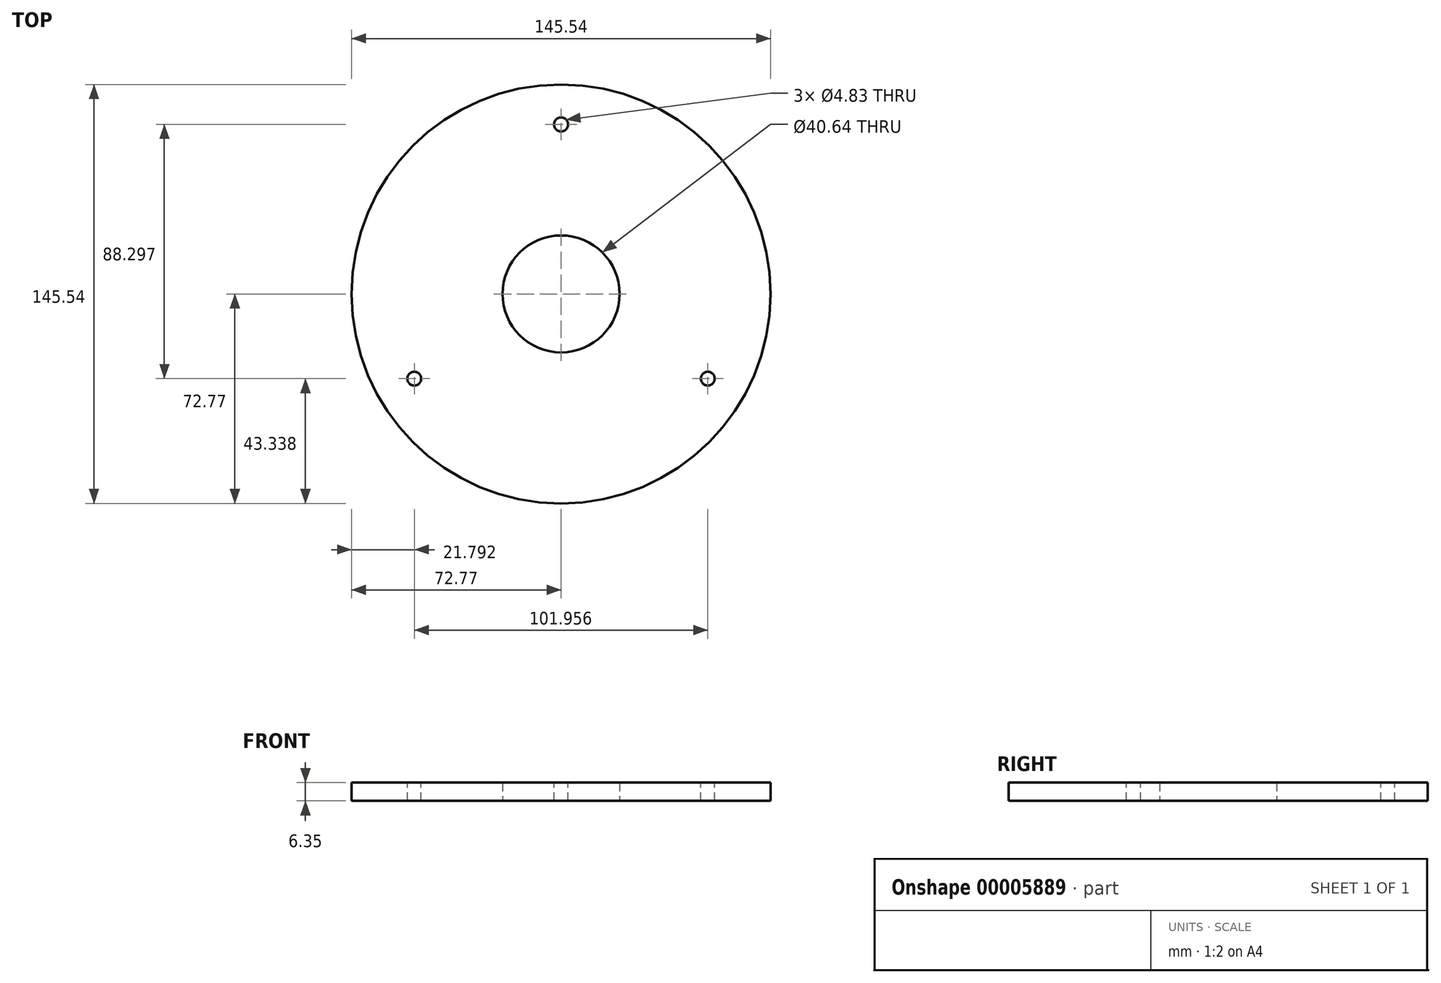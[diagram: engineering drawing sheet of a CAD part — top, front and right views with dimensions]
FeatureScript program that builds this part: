
annotation { "Feature Type Name" : "Feature", "Feature Type Description" : "" }
export const myFeature = defineFeature(function(context is Context, id is Id, definition is map)
    precondition{}
    {
        {
            var Q0;
            Q0=qCreatedBy(makeId("Top.planeOp"),FACE);
            var sketch = newSketch(context, id + "F0", { "sketchPlane" : qUnion([Q0])});
            skCircle(sketch, "E0", {"center": v(0, 0) * mm, "radius": 20.32 * mm});
            skLineSegment(sketch, "E1", {"start": v(0, 0) * mm, "end": v(-72.77, 0) * mm, "construction": true});
            skLineSegment(sketch, "E2", {"start": v(-72.77, 0) * mm, "end": v(-148.97, 0) * mm, "construction": true});
            skArc(sketch, "E3", {"start": v(-157.42, 43.64) * mm, "mid": v(-193.42, 0) * mm, "end": v(-157.42, -43.64) * mm});
            skCircle(sketch, "E4", {"center": v(-148.97, 0) * mm, "radius": 4.76 * mm});
            skCircle(sketch, "E5.converted", {"center": v(0, 0) * mm, "radius": 72.77 * mm});
            skSolve(sketch);
        }
        {
            var Q0;
            Q0=makeQuery(id+"F0.imprint","IMPRINT",FACE,{"disambiguationData":[TD([[makeQuery(id+"F0.imprint","IMPRINT",EDGE,{"derivedFrom":sQuery(id+"F0.wireOp",EDGE,"E0")}),-1.0]])]});
            extrude(context, id + "F1", {"entities" : qUnion([Q0]), "depth" : 6.35 * mm});
        }
        {
            var Q0;
            Q0=makeQuery(id+"F1.opExtrude","CAP_FACE",FACE,{"disambiguationData":[OSD([sQuery(id+"F0.wireOp",EDGE,"e6a074b3-585f-481e-9c95-f9684aebe7da"),sQuery(id+"F0.wireOp",EDGE,"E0"),sQuery(id+"F0.wireOp",EDGE,"7409aa68-249a-4d23-94e3-a1b410b62b42")])],"isStart":false});
            var sketch = newSketch(context, id + "F2", { "sketchPlane" : qUnion([Q0])});
            skLineSegment(sketch, "E6", {"start": v(0, 0) * mm, "end": v(0, 72.77) * mm, "construction": true});
            skCircle(sketch, "E7", {"center": v(0, 58.86) * mm, "radius": 4.76 * mm});
            skCircle(sketch, "E8.1.0", {"center": v(-50.98, -29.43) * mm, "radius": 4.76 * mm});
            skCircle(sketch, "E8.2.0", {"center": v(50.98, -29.43) * mm, "radius": 4.76 * mm});
            skPoint(sketch, "E8.center", {"position": v(0, 0) * mm});
            skCircle(sketch, "E9", {"center": v(0, 58.86) * mm, "radius": 2.41 * mm});
            skCircle(sketch, "E10.1.0", {"center": v(-50.98, -29.43) * mm, "radius": 2.41 * mm});
            skCircle(sketch, "E10.2.0", {"center": v(50.98, -29.43) * mm, "radius": 2.41 * mm});
            skSolve(sketch);
        }
        {
            var Q0;
            Q0=makeQuery(id+"F2.imprint","IMPRINT",FACE,{"disambiguationData":[TD([[makeQuery(id+"F2.imprint","IMPRINT",EDGE,{"derivedFrom":sQuery(id+"F2.wireOp",EDGE,"E10.1.0")}),1.0]])]});
            var Q1;
            Q1=makeQuery(id+"F2.imprint","IMPRINT",FACE,{"disambiguationData":[TD([[makeQuery(id+"F2.imprint","IMPRINT",EDGE,{"derivedFrom":sQuery(id+"F2.wireOp",EDGE,"E10.2.0")}),1.0]])]});
            var Q2;
            Q2=makeQuery(id+"F2.imprint","IMPRINT",FACE,{"disambiguationData":[TD([[makeQuery(id+"F2.imprint","IMPRINT",EDGE,{"derivedFrom":sQuery(id+"F2.wireOp",EDGE,"E9")}),1.0]])]});
            extrude(context, id + "F3", {"entities" : qUnion([Q0, Q1, Q2]), "operationType" : NewBodyOperationType.REMOVE, "endBound" : BoundingType.THROUGH_ALL, "oppositeDirection" : true, "depth" : 25.4 * mm});
        }
        {
            var Q0;
            Q0=makeQuery(id+"F1.opExtrude","CAP_FACE",FACE,{"disambiguationData":[OSD([sQuery(id+"F0.wireOp",EDGE,"e6a074b3-585f-481e-9c95-f9684aebe7da"),sQuery(id+"F0.wireOp",EDGE,"E0"),sQuery(id+"F0.wireOp",EDGE,"7409aa68-249a-4d23-94e3-a1b410b62b42")])],"isStart":false});
            var sketch = newSketch(context, id + "F4", { "sketchPlane" : qUnion([Q0])});
            skCircle(sketch, "E11", {"center": v(0, 0) * mm, "radius": 17.78 * mm});
            skSolve(sketch);
        }
        {
            var Q0;
            Q0=makeQuery(id+"F4.imprint","IMPRINT",FACE,{"disambiguationData":[TD([[makeQuery(id+"F4.imprint","IMPRINT",EDGE,{"derivedFrom":sQuery(id+"F4.wireOp",EDGE,"E11")}),1.0]])]});
            extrude(context, id + "F5", {"entities" : qUnion([Q0]), "operationType" : NewBodyOperationType.REMOVE, "oppositeDirection" : true, "depth" : 2.8 * mm});
        }
        {
            var Q0;
            Q0=makeQuery(id+"F1.opExtrude","CAP_FACE",FACE,{"disambiguationData":[OSD([sQuery(id+"F0.wireOp",EDGE,"e6a074b3-585f-481e-9c95-f9684aebe7da"),sQuery(id+"F0.wireOp",EDGE,"E0"),sQuery(id+"F0.wireOp",EDGE,"7409aa68-249a-4d23-94e3-a1b410b62b42")])],"isStart":true});
            var sketch = newSketch(context, id + "F6", { "sketchPlane" : qUnion([Q0])});
            skCircle(sketch, "E12", {"center": v(0, 0) * mm, "radius": 18.41 * mm});
            skSolve(sketch);
        }
        {
            var Q0;
            Q0=makeQuery(id+"F6.imprint","IMPRINT",FACE,{"disambiguationData":[TD([[makeQuery(id+"F6.imprint","IMPRINT",EDGE,{"derivedFrom":sQuery(id+"F6.wireOp",EDGE,"E12")}),1.0]])]});
            extrude(context, id + "F7", {"entities" : qUnion([Q0]), "operationType" : NewBodyOperationType.REMOVE, "oppositeDirection" : true, "depth" : 1.59 * mm});
        }
    });
